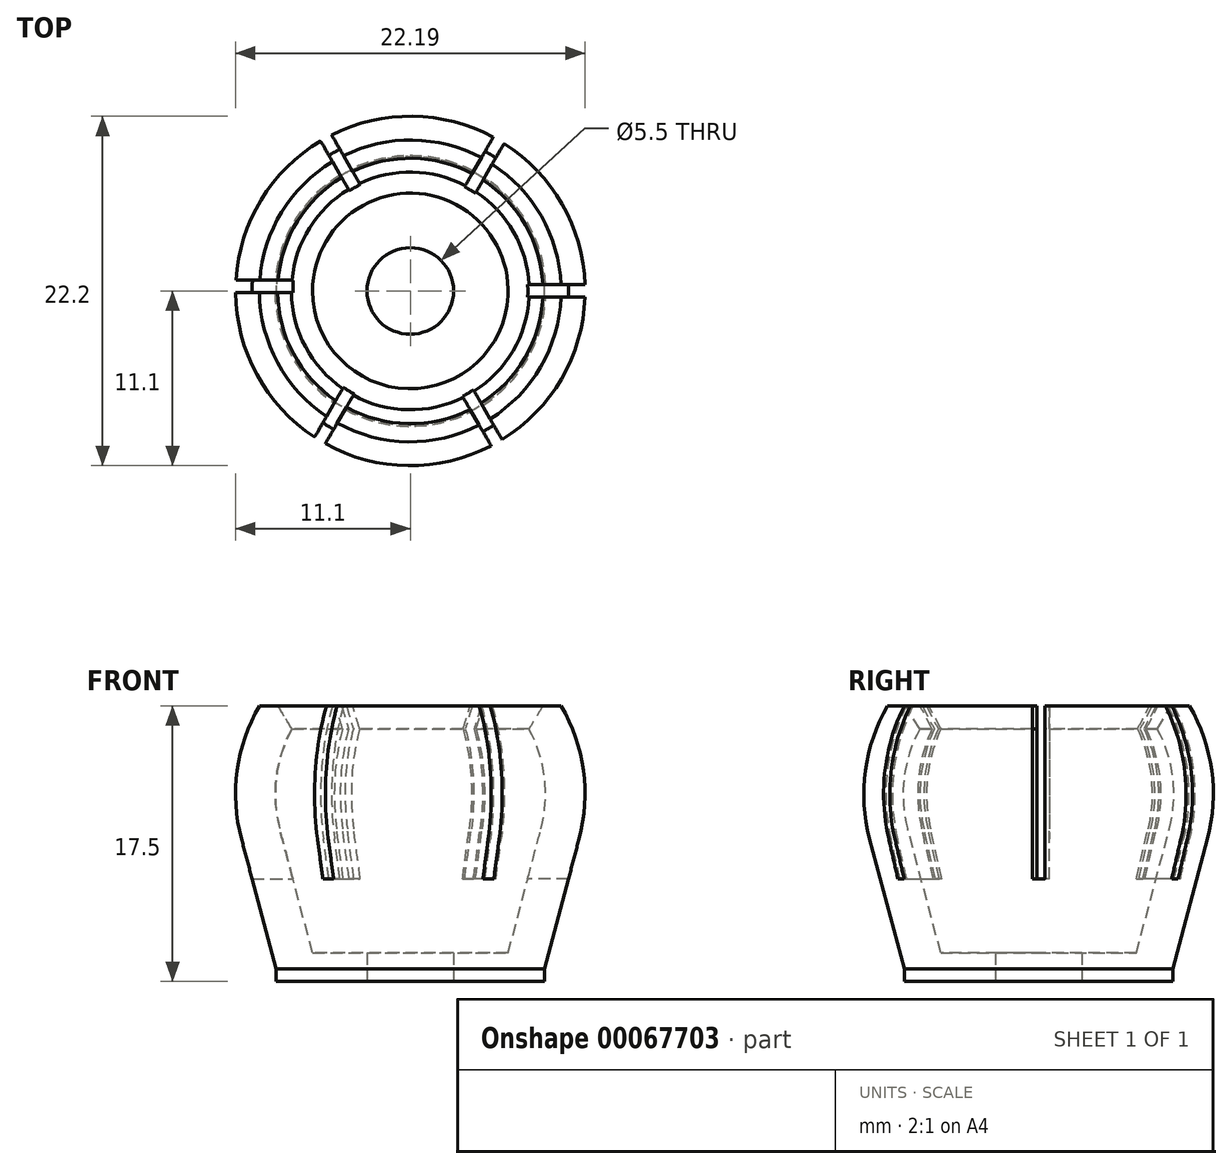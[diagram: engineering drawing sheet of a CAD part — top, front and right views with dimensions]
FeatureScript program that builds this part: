
annotation { "Feature Type Name" : "Feature", "Feature Type Description" : "" }
export const myFeature = defineFeature(function(context is Context, id is Id, definition is map)
    precondition{}
    {
        {
            var Q0;
            Q0=qCreatedBy(makeId("Front.planeOp"),FACE);
            var sketch = newSketch(context, id + "F0", { "sketchPlane" : qUnion([Q0])});
            skCircle(sketch, "E0", {"center": v(0, 0) * mm, "radius": 11.1 * mm, "construction": true});
            skArc(sketch, "E1", {"start": v(0, -11.1) * mm, "mid": v(11.1, 0) * mm, "end": v(0, 11.1) * mm});
            skLineSegment(sketch, "E2", {"start": v(0, -7.1) * mm, "end": v(8.53, -7.1) * mm, "construction": true});
            skLineSegment(sketch, "E3", {"start": v(8.53, -7.1) * mm, "end": v(8.53, -11.1) * mm, "construction": true});
            skLineSegment(sketch, "E4", {"start": v(8.53, -11.1) * mm, "end": v(0, -11.1) * mm});
            skLineSegment(sketch, "E5", {"start": v(9.58, 5.6) * mm, "end": v(0, 5.6) * mm});
            skLineSegment(sketch, "E6", {"start": v(0, 5.6) * mm, "end": v(0, -11.1) * mm});
            skLineSegment(sketch, "E7", {"start": v(10.73, -2.85) * mm, "end": v(8.53, -11.1) * mm});
            skLineSegment(sketch, "E8", {"start": v(9.58, 5.6) * mm, "end": v(9.58, 5.6) * mm});
            skSolve(sketch);
        }
        {
            var Q0;
            Q0=makeQuery(id+"F0.imprint","IMPRINT",FACE,{"disambiguationData":[TD([[makeQuery(id+"F0.imprint","IMPRINT",EDGE,{"derivedFrom":sQuery(id+"F0.wireOp",EDGE,"E5")}),1.0]])]});
            var Q1;
            {var subQ0=sQuery(id+"F0.wireOp",EDGE,"E4");Q1=makeQuery(id+"F0.imprint","IMPRINT",FACE,{"disambiguationData":[TD([[makeQuery(id+"F0.imprint","IMPRINT",EDGE,{"derivedFrom":subQ0}),-1.0]])]});}
            var Q2;
            Q2=sQuery(id+"F0.wireOp",EDGE,"E6");
            revolve(context, id + "F1", {"entities" : qUnion([Q0, Q1]), "axis" : qUnion([Q2]), "revolveType" : RevolveType.FULL});
        }
        {
            var Q0;
            Q0=makeQuery(id+"F1.opRevolve","SWEPT_FACE",FACE,{"disambiguationData":[OSD([sQuery(id+"F0.wireOp",EDGE,"E5")])]});
            var Q1;
            Q1=makeQuery(id+"F1.opRevolve","SWEPT_FACE",FACE,{"disambiguationData":[OSD([sQuery(id+"F0.wireOp",EDGE,"E4")])]});
            shell(context, id + "F2", {"entities" : qUnion([Q0, Q1]), "thickness" : 2.5 * mm});
        }
        {
            var Q0;
            Q0=makeQuery(id+"F1.opRevolve","SWEPT_FACE",FACE,{"disambiguationData":[OSD([sQuery(id+"F0.wireOp",EDGE,"E5")])]});
            var sketch = newSketch(context, id + "F3", { "sketchPlane" : qUnion([Q0])});
            skLineSegment(sketch, "E9.rect.bottom", {"start": v(12.5, 0.4) * mm, "end": v(-12.5, 0.4) * mm, "construction": true});
            skLineSegment(sketch, "E9.rect.top", {"start": v(12.5, -0.4) * mm, "end": v(-12.5, -0.4) * mm, "construction": true});
            skLineSegment(sketch, "E9.rect.left", {"start": v(12.5, 0.4) * mm, "end": v(12.5, -0.4) * mm, "construction": true});
            skLineSegment(sketch, "E9.rect.right", {"start": v(-12.5, 0.4) * mm, "end": v(-12.5, -0.4) * mm, "construction": true});
            skPoint(sketch, "E9.rect.middle", {"position": v(0, 0) * mm});
            skLineSegment(sketch, "E10.bottom", {"start": v(12.5, 0.4) * mm, "end": v(0, 0.4) * mm});
            skLineSegment(sketch, "E10.top", {"start": v(12.5, -0.4) * mm, "end": v(0, -0.4) * mm});
            skLineSegment(sketch, "E10.left", {"start": v(12.5, 0.4) * mm, "end": v(12.5, -0.4) * mm});
            skLineSegment(sketch, "E10.right", {"start": v(0, 0.4) * mm, "end": v(0, -0.4) * mm});
            skLineSegment(sketch, "E11.1.0", {"start": v(6.03, 11.1) * mm, "end": v(-0.22, 0.28) * mm});
            skLineSegment(sketch, "E11.1.1", {"start": v(6.03, 11.1) * mm, "end": v(6.73, 10.7) * mm});
            skLineSegment(sketch, "E11.1.2", {"start": v(6.73, 10.7) * mm, "end": v(0.48, -0.12) * mm});
            skLineSegment(sketch, "E11.1.3", {"start": v(-0.22, 0.28) * mm, "end": v(0.48, -0.12) * mm});
            skLineSegment(sketch, "E11.2.0", {"start": v(-6.47, 10.85) * mm, "end": v(-0.22, 0.03) * mm});
            skLineSegment(sketch, "E11.2.1", {"start": v(-6.47, 10.85) * mm, "end": v(-5.77, 11.25) * mm});
            skLineSegment(sketch, "E11.2.2", {"start": v(-5.77, 11.25) * mm, "end": v(0.48, 0.43) * mm});
            skLineSegment(sketch, "E11.2.3", {"start": v(-0.22, 0.03) * mm, "end": v(0.48, 0.43) * mm});
            skPoint(sketch, "E11.center", {"position": v(0, 0.15) * mm});
            skLineSegment(sketch, "E12.2.3.0", {"start": v(-12.5, -0.1) * mm, "end": v(0, -0.1) * mm});
            skLineSegment(sketch, "E12.3.3.0", {"start": v(-12.5, -0.1) * mm, "end": v(-12.5, 0.7) * mm});
            skLineSegment(sketch, "E12.6.3.0", {"start": v(-12.5, 0.7) * mm, "end": v(0, 0.7) * mm});
            skLineSegment(sketch, "E12.9.3.0", {"start": v(0, -0.1) * mm, "end": v(0, 0.7) * mm});
            skLineSegment(sketch, "E12.2.4.0", {"start": v(-6.03, -10.8) * mm, "end": v(0.22, 0.03) * mm});
            skLineSegment(sketch, "E12.3.4.0", {"start": v(-6.03, -10.8) * mm, "end": v(-6.73, -10.4) * mm});
            skLineSegment(sketch, "E12.6.4.0", {"start": v(-6.73, -10.4) * mm, "end": v(-0.48, 0.43) * mm});
            skLineSegment(sketch, "E12.9.4.0", {"start": v(0.22, 0.03) * mm, "end": v(-0.48, 0.43) * mm});
            skLineSegment(sketch, "E13.2.5.0", {"start": v(6.47, -10.55) * mm, "end": v(0.22, 0.28) * mm});
            skLineSegment(sketch, "E13.3.5.0", {"start": v(6.47, -10.55) * mm, "end": v(5.77, -10.95) * mm});
            skLineSegment(sketch, "E13.6.5.0", {"start": v(5.77, -10.95) * mm, "end": v(-0.48, -0.12) * mm});
            skLineSegment(sketch, "E13.9.5.0", {"start": v(0.22, 0.28) * mm, "end": v(-0.48, -0.12) * mm});
            skSolve(sketch);
        }
        {
            var Q0;
            Q0 = qSketchRegion(id + "F3", true);
            var Q1;
            {var subQ0=sQuery(id+"F3.wireOp",EDGE,"E10.right");var subQ1=sQuery(id+"F3.wireOp",EDGE,"E10.bottom");var subQ2=makeQuery(id+"F3.imprint","INTERSECT",VERTEX,{"derivedFrom":[subQ1,subQ0]});Q1=makeQuery(id+"F3.imprint","IMPRINT",FACE,{"disambiguationData":[TD([[makeQuery(id+"F3.imprint","IMPRINT",EDGE,{"disambiguationData":[TD([[subQ2,1.0]])],"derivedFrom":subQ1}),1.0]])]});}
            var Q2;
            {var subQ0=sQuery(id+"F3.wireOp",EDGE,"E11.1.3");var subQ1=sQuery(id+"F3.wireOp",EDGE,"E11.1.0");var subQ2=makeQuery(id+"F3.imprint","INTERSECT",VERTEX,{"derivedFrom":[subQ1,subQ0]});Q2=makeQuery(id+"F3.imprint","IMPRINT",FACE,{"disambiguationData":[TD([[makeQuery(id+"F3.imprint","IMPRINT",EDGE,{"disambiguationData":[TD([[subQ2,1.0]])],"derivedFrom":subQ1}),1.0]])]});}
            var Q3;
            {var subQ0=sQuery(id+"F3.wireOp",EDGE,"E11.2.3");var subQ1=sQuery(id+"F3.wireOp",EDGE,"E11.2.0");var subQ2=makeQuery(id+"F3.imprint","INTERSECT",VERTEX,{"derivedFrom":[subQ1,subQ0]});Q3=makeQuery(id+"F3.imprint","IMPRINT",FACE,{"disambiguationData":[TD([[makeQuery(id+"F3.imprint","IMPRINT",EDGE,{"disambiguationData":[TD([[subQ2,1.0]])],"derivedFrom":subQ1}),1.0]])]});}
            var Q4;
            {var subQ0=sQuery(id+"F3.wireOp",EDGE,"E10.right");var subQ1=sQuery(id+"F3.wireOp",EDGE,"E10.top");var subQ2=makeQuery(id+"F3.imprint","INTERSECT",VERTEX,{"derivedFrom":[subQ1,subQ0]});Q4=makeQuery(id+"F3.imprint","IMPRINT",FACE,{"disambiguationData":[TD([[makeQuery(id+"F3.imprint","IMPRINT",EDGE,{"disambiguationData":[TD([[subQ2,1.0]])],"derivedFrom":subQ1}),-1.0]])]});}
            var Q5;
            {var subQ0=sQuery(id+"F3.wireOp",EDGE,"E11.1.3");var subQ1=sQuery(id+"F3.wireOp",EDGE,"E11.1.2");var subQ2=makeQuery(id+"F3.imprint","INTERSECT",VERTEX,{"derivedFrom":[subQ1,subQ0]});Q5=makeQuery(id+"F3.imprint","IMPRINT",FACE,{"disambiguationData":[TD([[makeQuery(id+"F3.imprint","IMPRINT",EDGE,{"disambiguationData":[TD([[subQ2,1.0]])],"derivedFrom":subQ1}),-1.0]])]});}
            extrude(context, id + "F4", {"entities" : qUnion([Q0, Q1, Q2, Q3, Q4, Q5]), "operationType" : NewBodyOperationType.REMOVE, "oppositeDirection" : true, "depth" : 11 * mm});
        }
        {
            var Q0;
            {var subQ0=sQuery(id+"F0.wireOp",EDGE,"E5");var subQ1=sQuery(id+"F0.wireOp",EDGE,"E1");Q0=makeQuery(id+"F4.boolean.opBoolean","SPLIT",EDGE,{"disambiguationData":[TD([makeQuery(id+"F4.opExtrude","SWEPT_FACE",FACE,{"disambiguationData":[OSD([sQuery(id+"F3.wireOp",EDGE,"E11.1.0")])]})])],"derivedFrom":makeQuery(id+"F2.opShell","OFFSET_EDGE",EDGE,{"disambiguationData":[OSD([subQ1,subQ0])]})});}
            var Q1;
            {var subQ0=sQuery(id+"F0.wireOp",EDGE,"E5");var subQ1=sQuery(id+"F0.wireOp",EDGE,"E1");Q1=makeQuery(id+"F4.boolean.opBoolean","SPLIT",EDGE,{"disambiguationData":[TD([makeQuery(id+"F4.opExtrude","SWEPT_FACE",FACE,{"disambiguationData":[OSD([sQuery(id+"F3.wireOp",EDGE,"E10.bottom")])]})])],"derivedFrom":makeQuery(id+"F2.opShell","OFFSET_EDGE",EDGE,{"disambiguationData":[OSD([subQ1,subQ0])]})});}
            var Q2;
            {var subQ0=sQuery(id+"F0.wireOp",EDGE,"E5");var subQ1=sQuery(id+"F0.wireOp",EDGE,"E1");Q2=makeQuery(id+"F4.boolean.opBoolean","SPLIT",EDGE,{"disambiguationData":[TD([makeQuery(id+"F4.opExtrude","SWEPT_FACE",FACE,{"disambiguationData":[OSD([sQuery(id+"F3.wireOp",EDGE,"E10.top")])]})])],"derivedFrom":makeQuery(id+"F2.opShell","OFFSET_EDGE",EDGE,{"disambiguationData":[OSD([subQ1,subQ0])]})});}
            var Q3;
            {var subQ0=sQuery(id+"F0.wireOp",EDGE,"E5");var subQ1=sQuery(id+"F0.wireOp",EDGE,"E1");Q3=makeQuery(id+"F4.boolean.opBoolean","SPLIT",EDGE,{"disambiguationData":[TD([makeQuery(id+"F4.opExtrude","SWEPT_FACE",FACE,{"disambiguationData":[OSD([sQuery(id+"F3.wireOp",EDGE,"E11.2.0")])]})])],"derivedFrom":makeQuery(id+"F2.opShell","OFFSET_EDGE",EDGE,{"disambiguationData":[OSD([subQ1,subQ0])]})});}
            var Q4;
            {var subQ0=sQuery(id+"F0.wireOp",EDGE,"E5");var subQ1=sQuery(id+"F0.wireOp",EDGE,"E1");Q4=makeQuery(id+"F4.boolean.opBoolean","SPLIT",EDGE,{"disambiguationData":[TD([makeQuery(id+"F4.opExtrude","SWEPT_FACE",FACE,{"disambiguationData":[OSD([sQuery(id+"F3.wireOp",EDGE,"E12.2.3.0")])]})])],"derivedFrom":makeQuery(id+"F2.opShell","OFFSET_EDGE",EDGE,{"disambiguationData":[OSD([subQ1,subQ0])]})});}
            var Q5;
            {var subQ0=sQuery(id+"F0.wireOp",EDGE,"E5");var subQ1=sQuery(id+"F0.wireOp",EDGE,"E1");Q5=makeQuery(id+"F4.boolean.opBoolean","SPLIT",EDGE,{"disambiguationData":[TD([makeQuery(id+"F4.opExtrude","SWEPT_FACE",FACE,{"disambiguationData":[OSD([sQuery(id+"F3.wireOp",EDGE,"E12.2.4.0")])]})])],"derivedFrom":makeQuery(id+"F2.opShell","OFFSET_EDGE",EDGE,{"disambiguationData":[OSD([subQ1,subQ0])]})});}
            chamfer(context, id + "F5", {"entities" : qUnion([Q0, Q1, Q2, Q3, Q4, Q5]), "width" : 1 * mm, "tangentPropagation" : true});
        }
        {
            var Q0;
            Q0=makeQuery(id+"F1.opRevolve","SWEPT_FACE",FACE,{"disambiguationData":[OSD([sQuery(id+"F0.wireOp",EDGE,"E4")])]});
            var sketch = newSketch(context, id + "F6", { "sketchPlane" : qUnion([Q0])});
            skCircle(sketch, "E14.0", {"center": v(0, 0) * mm, "radius": 8.53 * mm});
            skCircle(sketch, "E15", {"center": v(0, 0) * mm, "radius": 2.75 * mm});
            skSolve(sketch);
        }
        {
            var Q0;
            Q0 = qSketchRegion(id + "F6", true);
            extrude(context, id + "F7", {"entities" : qUnion([Q0]), "operationType" : NewBodyOperationType.ADD, "oppositeDirection" : true, "depth" : 1 * mm, "hasSecondDirection" : true, "secondDirectionOppositeDirection" : false, "secondDirectionDepth" : .8 * mm});
        }
    });
